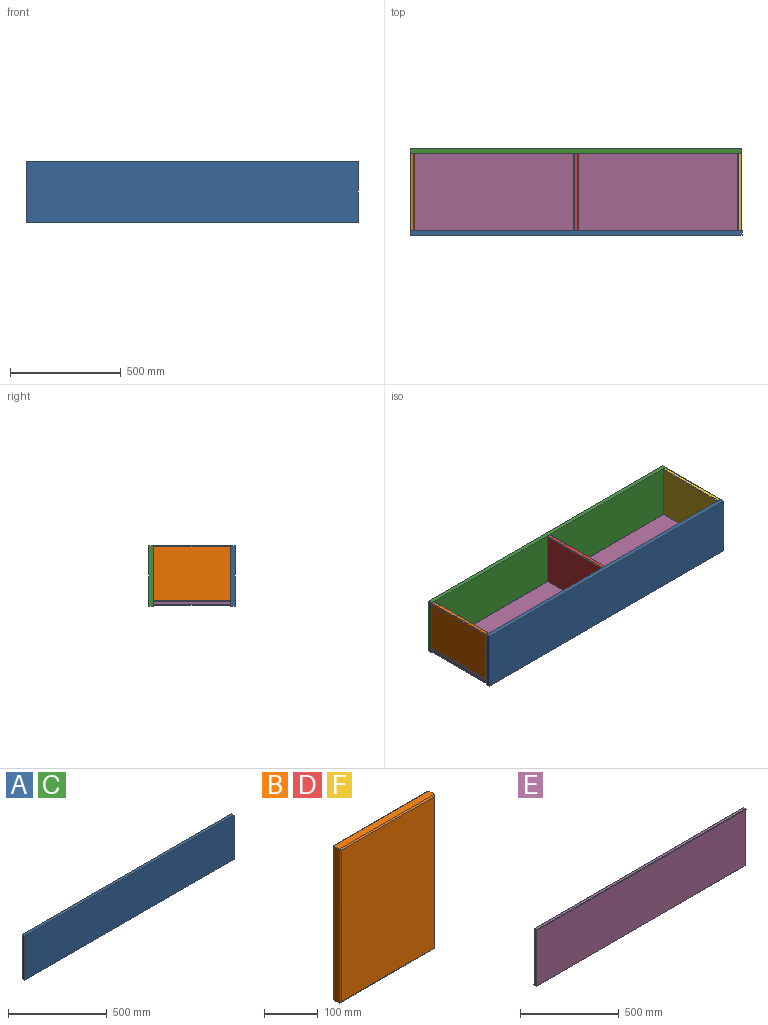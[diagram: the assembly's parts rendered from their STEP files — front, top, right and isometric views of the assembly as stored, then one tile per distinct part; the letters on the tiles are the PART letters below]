
ASSEMBLY  parts=6 mates=5
PART A: 6 faces, bbox 1500x20x275 mm
  f0: plane 275x20mm, normal (-1,0,0), area 5500mm2, adj f1,f3,f4,f5
  f1: plane 1500x20mm, normal (0,0,-1), area 30000mm2, adj f0,f2,f4,f5
  f2: plane 275x20mm, normal (1,0,0), area 5500mm2, adj f1,f3,f4,f5
  f3: plane 1500x20mm, normal (0,0,1), area 30000mm2, adj f0,f2,f4,f5
  f4: plane 1500x275mm, normal (0,-1,0), area 412500mm2, adj f0,f1,f2,f3
  f5: plane 1500x275mm, normal (0,1,0), area 412500mm2, adj f0,f1,f2,f3
PART B: 14 faces, bbox 250x20x350 mm
  f0: plane 350x14mm, normal (-1,0,0), area 4900mm2, adj f1,f3,f6,f10
  f1: plane 250x14mm, normal (0,0,-1), area 3500mm2, adj f0,f2,f8,f12
  f2: plane 350x14mm, normal (1,0,0), area 4900mm2, adj f1,f3,f9,f13
  f3: plane 250x14mm, normal (0,0,1), area 3500mm2, adj f0,f2,f7,f11
  f4: plane 344x244mm, normal (0,-1,0), area 83936mm2, adj f10,f11,f12,f13
  f5: plane 344x244mm, normal (0,1,0), area 83936mm2, adj f6,f7,f8,f9
  f6: cylinder r=3mm len=350mm, axis (0,0,-1), area 1639.1mm2, adj f0,f5,f7,f8
  f7: cylinder r=3mm len=250mm, axis (-1,0,0), area 1167.8mm2, adj f3,f5,f6,f9
  f8: cylinder r=3mm len=250mm, axis (1,0,0), area 1167.8mm2, adj f1,f5,f6,f9
  f9: cylinder r=3mm len=350mm, axis (0,0,1), area 1639.1mm2, adj f2,f5,f7,f8
  f10: cylinder r=3mm len=350mm, axis (0,0,1), area 1639.1mm2, adj f0,f4,f11,f12
  f11: cylinder r=3mm len=250mm, axis (1,0,0), area 1167.8mm2, adj f3,f4,f10,f13
  f12: cylinder r=3mm len=250mm, axis (-1,0,0), area 1167.8mm2, adj f1,f4,f10,f13
  f13: cylinder r=3mm len=350mm, axis (0,0,-1), area 1639.1mm2, adj f2,f4,f11,f12
PART C: same geometry as A
PART D: same geometry as B
PART E: 14 faces, bbox 1500x20x350 mm
  f0: plane 350x14mm, normal (-1,0,0), area 4900mm2, adj f1,f3,f6,f10
  f1: plane 1500x14mm, normal (0,0,-1), area 21000mm2, adj f0,f2,f8,f12
  f2: plane 350x14mm, normal (1,0,0), area 4900mm2, adj f1,f3,f9,f13
  f3: plane 1500x14mm, normal (0,0,1), area 21000mm2, adj f0,f2,f7,f11
  f4: plane 1494x344mm, normal (0,-1,0), area 513936mm2, adj f10,f11,f12,f13
  f5: plane 1494x344mm, normal (0,1,0), area 513936mm2, adj f6,f7,f8,f9
  f6: cylinder r=3mm len=350mm, axis (0,0,-1), area 1639.1mm2, adj f0,f5,f7,f8
  f7: cylinder r=3mm len=1500mm, axis (-1,0,0), area 7058.3mm2, adj f3,f5,f6,f9
  f8: cylinder r=3mm len=1500mm, axis (1,0,0), area 7058.3mm2, adj f1,f5,f6,f9
  f9: cylinder r=3mm len=350mm, axis (0,0,1), area 1639.1mm2, adj f2,f5,f7,f8
  f10: cylinder r=3mm len=350mm, axis (0,0,1), area 1639.1mm2, adj f0,f4,f11,f12
  f11: cylinder r=3mm len=1500mm, axis (1,0,0), area 7058.3mm2, adj f3,f4,f10,f13
  f12: cylinder r=3mm len=1500mm, axis (-1,0,0), area 7058.3mm2, adj f1,f4,f10,f13
  f13: cylinder r=3mm len=350mm, axis (0,0,-1), area 1639.1mm2, adj f2,f4,f11,f12
PART F: same geometry as B
PLACE A rot(axis=(0,0,1),180deg) t=(796.82,-385.85,-159.93)mm
PLACE B rot(axis=(-0.58,0.58,0.58),120deg) t=(-561.28,-209.61,-224.28)mm
PLACE C t=(-419.38,4.15,-159.93)mm
PLACE D rot(axis=(0.58,0.58,-0.58),120deg) t=(198.72,-172.08,-224.28)mm
PLACE E rot(axis=(1,0,0),90deg) t=(-282.3,-178.56,-272.21)mm
PLACE F rot(axis=(0.58,0.58,-0.58),120deg) t=(938.72,-172.08,-224.28)mm
MATE fastened E.f1 <-> C.f4  axis (0,1,0) through (188.72,-15.85,-282.21)mm
MATE fastened F.f1 <-> C.f4  axis (0,1,0) through (928.72,-15.85,-72.21)mm
MATE fastened B.f3 <-> C.f4  axis (0,1,0) through (-551.28,-15.85,-72.21)mm
MATE fastened D.f1 <-> C.f4  axis (0,1,0) through (188.72,-15.85,-72.21)mm
MATE fastened A.f4 <-> D.f3  axis (0,1,0) through (188.72,-365.85,-72.21)mm
